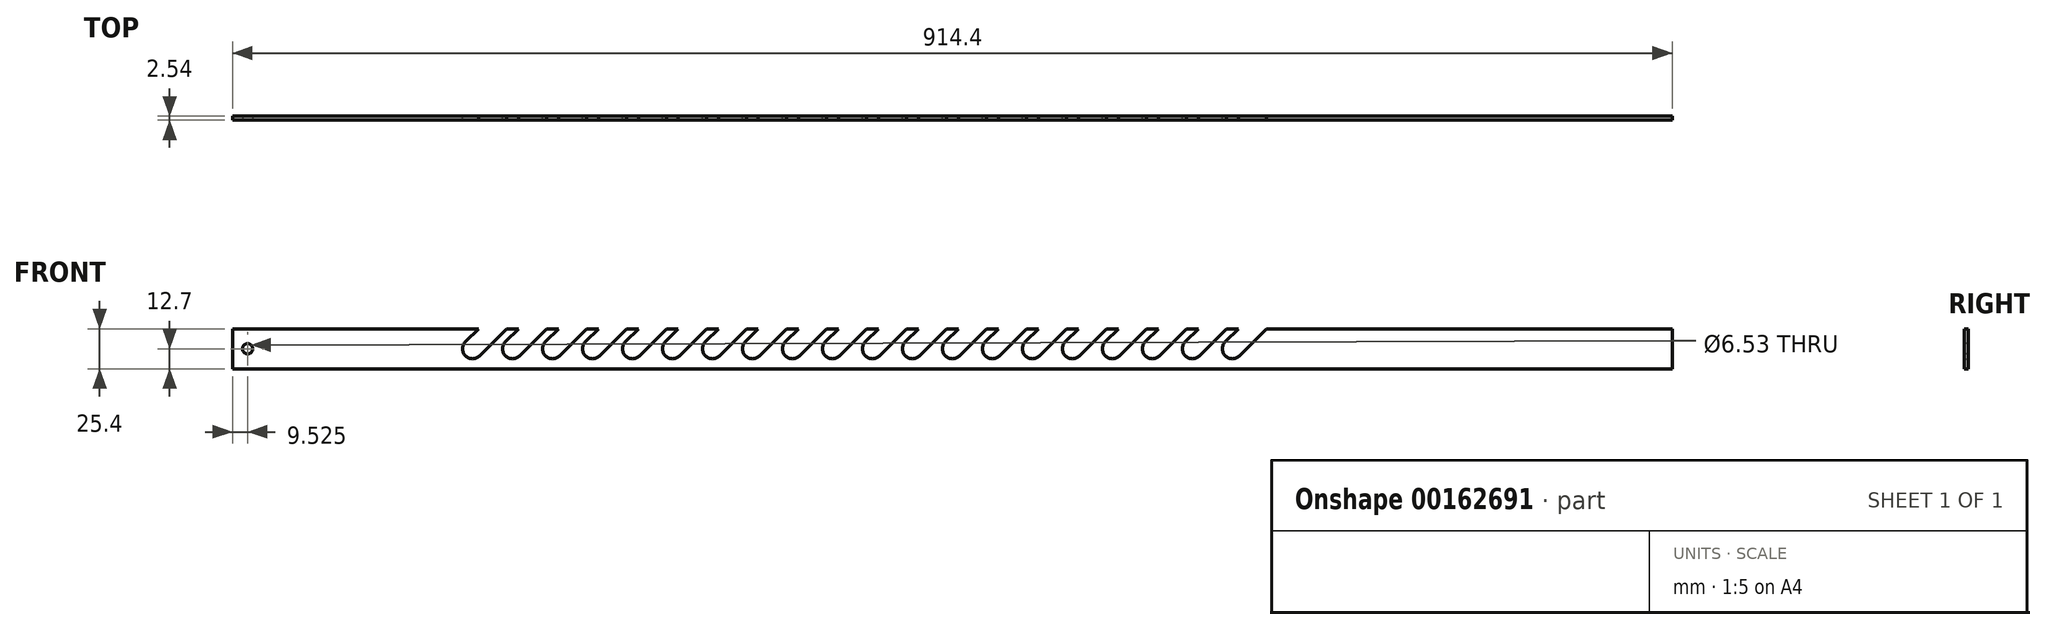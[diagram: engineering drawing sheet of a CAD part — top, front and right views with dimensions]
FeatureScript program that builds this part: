
annotation { "Feature Type Name" : "Feature", "Feature Type Description" : "" }
export const myFeature = defineFeature(function(context is Context, id is Id, definition is map)
    precondition{}
    {
        {
            var Q0;
            Q0=qCreatedBy(makeId("Front.planeOp"),FACE);
            var sketch = newSketch(context, id + "F0", { "sketchPlane" : qUnion([Q0])});
            skLineSegment(sketch, "E0.bottom", {"start": v(0, 0) * mm, "end": v(914.4, 0) * mm});
            skLineSegment(sketch, "E0.top", {"start": v(0, 25.4) * mm, "end": v(156.12, 25.4) * mm});
            skLineSegment(sketch, "E0.left", {"start": v(0, 0) * mm, "end": v(0, 25.4) * mm});
            skLineSegment(sketch, "E0.right", {"start": v(914.4, 0) * mm, "end": v(914.4, 25.4) * mm});
            skArc(sketch, "E1", {"start": v(147.9, 17.2) * mm, "mid": v(147.9, 8.2) * mm, "end": v(156.9, 8.2) * mm});
            skArc(sketch, "E2.1.0.0", {"start": v(173.3, 17.2) * mm, "mid": v(173.3, 8.2) * mm, "end": v(182.3, 8.2) * mm});
            skArc(sketch, "E2.2.0.0", {"start": v(198.7, 17.2) * mm, "mid": v(198.7, 8.2) * mm, "end": v(207.7, 8.2) * mm});
            skArc(sketch, "E2.3.0.0", {"start": v(224.1, 17.2) * mm, "mid": v(224.1, 8.2) * mm, "end": v(233.1, 8.2) * mm});
            skArc(sketch, "E2.4.0.0", {"start": v(249.5, 17.2) * mm, "mid": v(249.5, 8.2) * mm, "end": v(258.5, 8.2) * mm});
            skArc(sketch, "E2.5.0.0", {"start": v(274.9, 17.2) * mm, "mid": v(274.9, 8.2) * mm, "end": v(283.9, 8.2) * mm});
            skArc(sketch, "E2.6.0.0", {"start": v(300.3, 17.2) * mm, "mid": v(300.3, 8.2) * mm, "end": v(309.3, 8.2) * mm});
            skArc(sketch, "E2.7.0.0", {"start": v(325.7, 17.2) * mm, "mid": v(325.7, 8.2) * mm, "end": v(334.7, 8.2) * mm});
            skArc(sketch, "E2.8.0.0", {"start": v(351.1, 17.2) * mm, "mid": v(351.1, 8.2) * mm, "end": v(360.1, 8.2) * mm});
            skArc(sketch, "E2.9.0.0", {"start": v(376.5, 17.2) * mm, "mid": v(376.5, 8.2) * mm, "end": v(385.5, 8.2) * mm});
            skArc(sketch, "E2.10.0.0", {"start": v(401.9, 17.2) * mm, "mid": v(401.9, 8.2) * mm, "end": v(410.9, 8.2) * mm});
            skArc(sketch, "E2.11.0.0", {"start": v(427.3, 17.2) * mm, "mid": v(427.3, 8.2) * mm, "end": v(436.3, 8.2) * mm});
            skArc(sketch, "E2.12.0.0", {"start": v(452.7, 17.2) * mm, "mid": v(452.7, 8.2) * mm, "end": v(461.7, 8.2) * mm});
            skArc(sketch, "E2.13.0.0", {"start": v(478.1, 17.2) * mm, "mid": v(478.1, 8.2) * mm, "end": v(487.1, 8.2) * mm});
            skArc(sketch, "E2.14.0.0", {"start": v(503.5, 17.2) * mm, "mid": v(503.5, 8.2) * mm, "end": v(512.5, 8.2) * mm});
            skArc(sketch, "E2.15.0.0", {"start": v(528.9, 17.2) * mm, "mid": v(528.9, 8.2) * mm, "end": v(537.9, 8.2) * mm});
            skArc(sketch, "E2.16.0.0", {"start": v(554.3, 17.2) * mm, "mid": v(554.3, 8.2) * mm, "end": v(563.3, 8.2) * mm});
            skArc(sketch, "E2.17.0.0", {"start": v(579.7, 17.2) * mm, "mid": v(579.7, 8.2) * mm, "end": v(588.7, 8.2) * mm});
            skArc(sketch, "E2.18.0.0", {"start": v(605.1, 17.2) * mm, "mid": v(605.1, 8.2) * mm, "end": v(614.1, 8.2) * mm});
            skArc(sketch, "E2.19.0.0", {"start": v(630.5, 17.2) * mm, "mid": v(630.5, 8.2) * mm, "end": v(639.5, 8.2) * mm});
            skLineSegment(sketch, "E2.direction1", {"start": v(152.4, 12.7) * mm, "end": v(177.8, 12.7) * mm, "construction": true});
            skLineSegment(sketch, "E3", {"start": v(147.9, 17.2) * mm, "end": v(156.12, 25.4) * mm});
            skLineSegment(sketch, "E4.1.0.0", {"start": v(173.3, 17.2) * mm, "end": v(181.52, 25.4) * mm});
            skLineSegment(sketch, "E4.2.0.0", {"start": v(198.7, 17.2) * mm, "end": v(206.92, 25.4) * mm});
            skLineSegment(sketch, "E4.3.0.0", {"start": v(224.1, 17.2) * mm, "end": v(232.32, 25.4) * mm});
            skLineSegment(sketch, "E4.4.0.0", {"start": v(249.5, 17.2) * mm, "end": v(257.72, 25.4) * mm});
            skLineSegment(sketch, "E4.5.0.0", {"start": v(274.9, 17.2) * mm, "end": v(283.12, 25.4) * mm});
            skLineSegment(sketch, "E4.6.0.0", {"start": v(300.3, 17.2) * mm, "end": v(308.52, 25.4) * mm});
            skLineSegment(sketch, "E4.7.0.0", {"start": v(325.7, 17.2) * mm, "end": v(333.92, 25.4) * mm});
            skLineSegment(sketch, "E4.8.0.0", {"start": v(351.1, 17.2) * mm, "end": v(359.32, 25.4) * mm});
            skLineSegment(sketch, "E4.9.0.0", {"start": v(376.5, 17.2) * mm, "end": v(384.72, 25.4) * mm});
            skLineSegment(sketch, "E4.10.0.0", {"start": v(401.9, 17.2) * mm, "end": v(410.12, 25.4) * mm});
            skLineSegment(sketch, "E4.11.0.0", {"start": v(427.3, 17.2) * mm, "end": v(435.52, 25.4) * mm});
            skLineSegment(sketch, "E4.12.0.0", {"start": v(452.7, 17.2) * mm, "end": v(460.92, 25.4) * mm});
            skLineSegment(sketch, "E4.13.0.0", {"start": v(478.1, 17.2) * mm, "end": v(486.32, 25.4) * mm});
            skLineSegment(sketch, "E4.14.0.0", {"start": v(503.5, 17.2) * mm, "end": v(511.72, 25.4) * mm});
            skLineSegment(sketch, "E4.15.0.0", {"start": v(528.9, 17.2) * mm, "end": v(537.12, 25.4) * mm});
            skLineSegment(sketch, "E4.16.0.0", {"start": v(554.3, 17.2) * mm, "end": v(562.52, 25.4) * mm});
            skLineSegment(sketch, "E4.17.0.0", {"start": v(579.7, 17.2) * mm, "end": v(587.92, 25.4) * mm});
            skLineSegment(sketch, "E4.18.0.0", {"start": v(605.1, 17.2) * mm, "end": v(613.32, 25.4) * mm});
            skLineSegment(sketch, "E4.19.0.0", {"start": v(630.5, 17.2) * mm, "end": v(638.72, 25.4) * mm});
            skLineSegment(sketch, "E4.direction1", {"start": v(147.9, 17.2) * mm, "end": v(173.3, 17.2) * mm, "construction": true});
            skLineSegment(sketch, "E5", {"start": v(156.9, 8.2) * mm, "end": v(174.08, 25.4) * mm});
            skLineSegment(sketch, "E6.1.0.0", {"start": v(182.3, 8.2) * mm, "end": v(199.48, 25.4) * mm});
            skLineSegment(sketch, "E6.2.0.0", {"start": v(207.7, 8.2) * mm, "end": v(224.88, 25.4) * mm});
            skLineSegment(sketch, "E6.3.0.0", {"start": v(233.1, 8.2) * mm, "end": v(250.28, 25.4) * mm});
            skLineSegment(sketch, "E6.4.0.0", {"start": v(258.5, 8.2) * mm, "end": v(275.68, 25.4) * mm});
            skLineSegment(sketch, "E6.5.0.0", {"start": v(283.9, 8.2) * mm, "end": v(301.08, 25.4) * mm});
            skLineSegment(sketch, "E6.6.0.0", {"start": v(309.3, 8.2) * mm, "end": v(326.48, 25.4) * mm});
            skLineSegment(sketch, "E6.7.0.0", {"start": v(334.7, 8.2) * mm, "end": v(351.88, 25.4) * mm});
            skLineSegment(sketch, "E6.8.0.0", {"start": v(360.1, 8.2) * mm, "end": v(377.28, 25.4) * mm});
            skLineSegment(sketch, "E6.9.0.0", {"start": v(385.5, 8.2) * mm, "end": v(402.68, 25.4) * mm});
            skLineSegment(sketch, "E6.10.0.0", {"start": v(410.9, 8.2) * mm, "end": v(428.08, 25.4) * mm});
            skLineSegment(sketch, "E6.11.0.0", {"start": v(436.3, 8.2) * mm, "end": v(453.48, 25.4) * mm});
            skLineSegment(sketch, "E6.12.0.0", {"start": v(461.7, 8.2) * mm, "end": v(478.88, 25.4) * mm});
            skLineSegment(sketch, "E6.13.0.0", {"start": v(487.1, 8.2) * mm, "end": v(504.28, 25.4) * mm});
            skLineSegment(sketch, "E6.14.0.0", {"start": v(512.5, 8.2) * mm, "end": v(529.68, 25.4) * mm});
            skLineSegment(sketch, "E6.15.0.0", {"start": v(537.9, 8.2) * mm, "end": v(555.08, 25.4) * mm});
            skLineSegment(sketch, "E6.16.0.0", {"start": v(563.3, 8.2) * mm, "end": v(580.48, 25.4) * mm});
            skLineSegment(sketch, "E6.17.0.0", {"start": v(588.7, 8.2) * mm, "end": v(605.88, 25.4) * mm});
            skLineSegment(sketch, "E6.18.0.0", {"start": v(614.1, 8.2) * mm, "end": v(631.28, 25.4) * mm});
            skLineSegment(sketch, "E6.19.0.0", {"start": v(639.5, 8.2) * mm, "end": v(656.68, 25.4) * mm});
            skLineSegment(sketch, "E6.direction1", {"start": v(156.9, 8.2) * mm, "end": v(182.3, 8.2) * mm, "construction": true});
            skLineSegment(sketch, "E7.trimOffspring", {"start": v(174.08, 25.4) * mm, "end": v(181.52, 25.4) * mm});
            skLineSegment(sketch, "E8.trimOffspring", {"start": v(199.48, 25.4) * mm, "end": v(206.92, 25.4) * mm});
            skLineSegment(sketch, "E9.trimOffspring", {"start": v(224.88, 25.4) * mm, "end": v(232.32, 25.4) * mm});
            skLineSegment(sketch, "E10.trimOffspring", {"start": v(250.28, 25.4) * mm, "end": v(257.72, 25.4) * mm});
            skLineSegment(sketch, "E11.trimOffspring", {"start": v(275.68, 25.4) * mm, "end": v(283.12, 25.4) * mm});
            skLineSegment(sketch, "E12.trimOffspring", {"start": v(301.08, 25.4) * mm, "end": v(308.52, 25.4) * mm});
            skLineSegment(sketch, "E13.trimOffspring", {"start": v(326.48, 25.4) * mm, "end": v(333.92, 25.4) * mm});
            skLineSegment(sketch, "E14.trimOffspring", {"start": v(351.88, 25.4) * mm, "end": v(359.32, 25.4) * mm});
            skLineSegment(sketch, "E15.trimOffspring", {"start": v(377.28, 25.4) * mm, "end": v(384.72, 25.4) * mm});
            skLineSegment(sketch, "E16.trimOffspring", {"start": v(402.68, 25.4) * mm, "end": v(410.12, 25.4) * mm});
            skLineSegment(sketch, "E17.trimOffspring", {"start": v(428.08, 25.4) * mm, "end": v(435.52, 25.4) * mm});
            skLineSegment(sketch, "E18.trimOffspring", {"start": v(453.48, 25.4) * mm, "end": v(460.92, 25.4) * mm});
            skLineSegment(sketch, "E19.trimOffspring", {"start": v(478.88, 25.4) * mm, "end": v(486.32, 25.4) * mm});
            skLineSegment(sketch, "E20.trimOffspring", {"start": v(504.28, 25.4) * mm, "end": v(511.72, 25.4) * mm});
            skLineSegment(sketch, "E21.trimOffspring", {"start": v(529.68, 25.4) * mm, "end": v(537.12, 25.4) * mm});
            skLineSegment(sketch, "E22.trimOffspring", {"start": v(555.08, 25.4) * mm, "end": v(562.52, 25.4) * mm});
            skLineSegment(sketch, "E23.trimOffspring", {"start": v(580.48, 25.4) * mm, "end": v(587.92, 25.4) * mm});
            skLineSegment(sketch, "E24.trimOffspring", {"start": v(605.88, 25.4) * mm, "end": v(613.32, 25.4) * mm});
            skLineSegment(sketch, "E25.trimOffspring", {"start": v(631.28, 25.4) * mm, "end": v(638.72, 25.4) * mm});
            skLineSegment(sketch, "E26.trimOffspring", {"start": v(656.68, 25.4) * mm, "end": v(914.4, 25.4) * mm});
            skSolve(sketch);
        }
        {
            var Q0;
            Q0 = qSketchRegion(id + "F0", true);
            extrude(context, id + "F1", {"entities" : qUnion([Q0]), "depth" : 2.54 * mm});
        }
        {
            var Q0;
            Q0=makeQuery(id+"F1.opExtrude","CAP_FACE",FACE,{"disambiguationData":[OSD([sQuery(id+"F0.wireOp",EDGE,"E0.bottom"),sQuery(id+"F0.wireOp",EDGE,"E0.top"),sQuery(id+"F0.wireOp",EDGE,"E0.left"),sQuery(id+"F0.wireOp",EDGE,"E0.right"),sQuery(id+"F0.wireOp",EDGE,"E1"),sQuery(id+"F0.wireOp",EDGE,"E2.1.0.0"),sQuery(id+"F0.wireOp",EDGE,"E2.2.0.0"),sQuery(id+"F0.wireOp",EDGE,"E2.3.0.0"),sQuery(id+"F0.wireOp",EDGE,"E2.4.0.0"),sQuery(id+"F0.wireOp",EDGE,"E2.5.0.0"),sQuery(id+"F0.wireOp",EDGE,"E2.6.0.0"),sQuery(id+"F0.wireOp",EDGE,"E2.7.0.0"),sQuery(id+"F0.wireOp",EDGE,"E2.8.0.0"),sQuery(id+"F0.wireOp",EDGE,"E2.9.0.0"),sQuery(id+"F0.wireOp",EDGE,"E2.10.0.0"),sQuery(id+"F0.wireOp",EDGE,"E2.11.0.0"),sQuery(id+"F0.wireOp",EDGE,"E2.12.0.0"),sQuery(id+"F0.wireOp",EDGE,"E2.13.0.0"),sQuery(id+"F0.wireOp",EDGE,"E2.14.0.0"),sQuery(id+"F0.wireOp",EDGE,"E2.15.0.0"),sQuery(id+"F0.wireOp",EDGE,"E2.16.0.0"),sQuery(id+"F0.wireOp",EDGE,"E2.17.0.0"),sQuery(id+"F0.wireOp",EDGE,"E2.18.0.0"),sQuery(id+"F0.wireOp",EDGE,"E2.19.0.0"),sQuery(id+"F0.wireOp",EDGE,"E3"),sQuery(id+"F0.wireOp",EDGE,"E4.1.0.0"),sQuery(id+"F0.wireOp",EDGE,"E4.2.0.0"),sQuery(id+"F0.wireOp",EDGE,"E4.3.0.0"),sQuery(id+"F0.wireOp",EDGE,"E4.4.0.0"),sQuery(id+"F0.wireOp",EDGE,"E4.5.0.0"),sQuery(id+"F0.wireOp",EDGE,"E4.6.0.0"),sQuery(id+"F0.wireOp",EDGE,"E4.7.0.0"),sQuery(id+"F0.wireOp",EDGE,"E4.8.0.0"),sQuery(id+"F0.wireOp",EDGE,"E4.9.0.0"),sQuery(id+"F0.wireOp",EDGE,"E4.10.0.0"),sQuery(id+"F0.wireOp",EDGE,"E4.11.0.0"),sQuery(id+"F0.wireOp",EDGE,"E4.12.0.0"),sQuery(id+"F0.wireOp",EDGE,"E4.13.0.0"),sQuery(id+"F0.wireOp",EDGE,"E4.14.0.0"),sQuery(id+"F0.wireOp",EDGE,"E4.15.0.0"),sQuery(id+"F0.wireOp",EDGE,"E4.16.0.0"),sQuery(id+"F0.wireOp",EDGE,"E4.17.0.0"),sQuery(id+"F0.wireOp",EDGE,"E4.18.0.0"),sQuery(id+"F0.wireOp",EDGE,"E4.19.0.0"),sQuery(id+"F0.wireOp",EDGE,"E5"),sQuery(id+"F0.wireOp",EDGE,"E6.1.0.0"),sQuery(id+"F0.wireOp",EDGE,"E6.2.0.0"),sQuery(id+"F0.wireOp",EDGE,"E6.3.0.0"),sQuery(id+"F0.wireOp",EDGE,"E6.4.0.0"),sQuery(id+"F0.wireOp",EDGE,"E6.5.0.0"),sQuery(id+"F0.wireOp",EDGE,"E6.6.0.0"),sQuery(id+"F0.wireOp",EDGE,"E6.7.0.0"),sQuery(id+"F0.wireOp",EDGE,"E6.8.0.0"),sQuery(id+"F0.wireOp",EDGE,"E6.9.0.0"),sQuery(id+"F0.wireOp",EDGE,"E6.10.0.0"),sQuery(id+"F0.wireOp",EDGE,"E6.11.0.0"),sQuery(id+"F0.wireOp",EDGE,"E6.12.0.0"),sQuery(id+"F0.wireOp",EDGE,"E6.13.0.0"),sQuery(id+"F0.wireOp",EDGE,"E6.14.0.0"),sQuery(id+"F0.wireOp",EDGE,"E6.15.0.0"),sQuery(id+"F0.wireOp",EDGE,"E6.16.0.0"),sQuery(id+"F0.wireOp",EDGE,"E6.17.0.0"),sQuery(id+"F0.wireOp",EDGE,"E6.18.0.0"),sQuery(id+"F0.wireOp",EDGE,"E6.19.0.0"),sQuery(id+"F0.wireOp",EDGE,"E7.trimOffspring"),sQuery(id+"F0.wireOp",EDGE,"E8.trimOffspring"),sQuery(id+"F0.wireOp",EDGE,"E9.trimOffspring"),sQuery(id+"F0.wireOp",EDGE,"E10.trimOffspring"),sQuery(id+"F0.wireOp",EDGE,"E11.trimOffspring"),sQuery(id+"F0.wireOp",EDGE,"E12.trimOffspring"),sQuery(id+"F0.wireOp",EDGE,"E13.trimOffspring"),sQuery(id+"F0.wireOp",EDGE,"E14.trimOffspring"),sQuery(id+"F0.wireOp",EDGE,"E15.trimOffspring"),sQuery(id+"F0.wireOp",EDGE,"E16.trimOffspring"),sQuery(id+"F0.wireOp",EDGE,"E17.trimOffspring"),sQuery(id+"F0.wireOp",EDGE,"E18.trimOffspring"),sQuery(id+"F0.wireOp",EDGE,"E19.trimOffspring"),sQuery(id+"F0.wireOp",EDGE,"E20.trimOffspring"),sQuery(id+"F0.wireOp",EDGE,"E21.trimOffspring"),sQuery(id+"F0.wireOp",EDGE,"E22.trimOffspring"),sQuery(id+"F0.wireOp",EDGE,"E23.trimOffspring"),sQuery(id+"F0.wireOp",EDGE,"E24.trimOffspring"),sQuery(id+"F0.wireOp",EDGE,"E25.trimOffspring"),sQuery(id+"F0.wireOp",EDGE,"E26.trimOffspring")])],"isStart":false});
            var sketch = newSketch(context, id + "F2", { "sketchPlane" : qUnion([Q0])});
            skCircle(sketch, "E27", {"center": v(9.53, 12.7) * mm, "radius": 3.26 * mm});
            skSolve(sketch);
        }
        {
            var Q0;
            Q0 = qSketchRegion(id + "F2", true);
            extrude(context, id + "F3", {"entities" : qUnion([Q0]), "operationType" : NewBodyOperationType.REMOVE, "endBound" : BoundingType.THROUGH_ALL, "oppositeDirection" : true, "depth" : 25.4 * mm});
        }
    });
